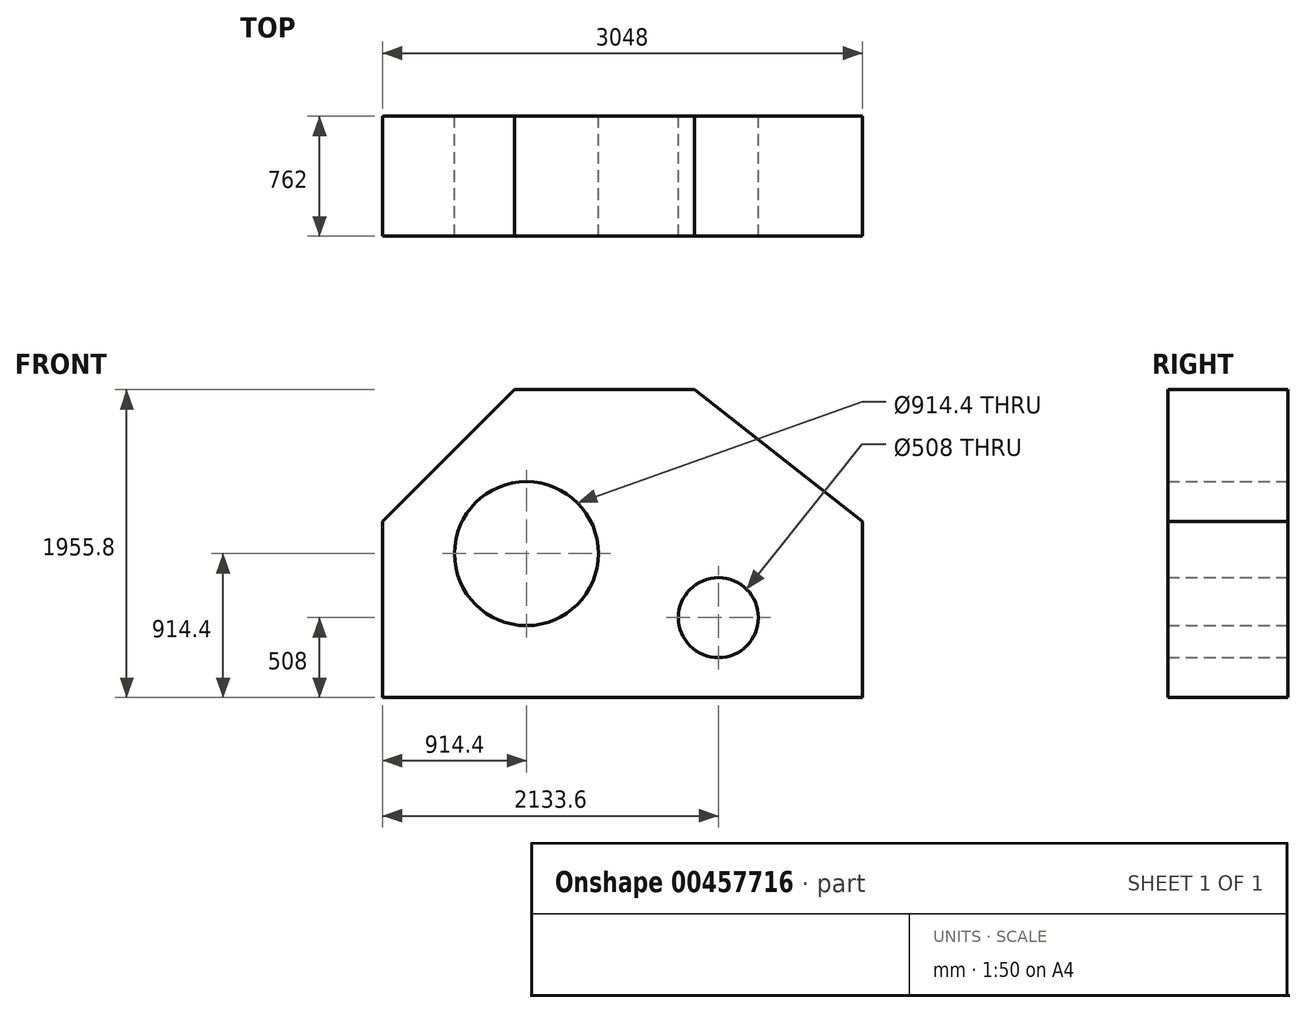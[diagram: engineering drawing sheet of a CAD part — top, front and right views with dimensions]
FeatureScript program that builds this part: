
annotation { "Feature Type Name" : "Feature", "Feature Type Description" : "" }
export const myFeature = defineFeature(function(context is Context, id is Id, definition is map)
    precondition{}
    {
        {
            var Q0;
            Q0=qCreatedBy(makeId("Front.planeOp"),FACE);
            var sketch = newSketch(context, id + "F0", { "sketchPlane" : qUnion([Q0])});
            skLineSegment(sketch, "E0", {"start": v(0, 0) * mm, "end": v(3048, 0) * mm});
            skLineSegment(sketch, "E1", {"start": v(3048, 0) * mm, "end": v(3048, 1117.6) * mm});
            skLineSegment(sketch, "E2", {"start": v(0, 0) * mm, "end": v(0, 1117.6) * mm});
            skLineSegment(sketch, "E3", {"start": v(0, 1117.6) * mm, "end": v(838.2, 1955.8) * mm});
            skLineSegment(sketch, "E4", {"start": v(838.2, 1955.8) * mm, "end": v(1981.2, 1955.8) * mm});
            skLineSegment(sketch, "E5", {"start": v(1981.2, 1955.8) * mm, "end": v(3048, 1117.6) * mm});
            skCircle(sketch, "E6", {"center": v(914.4, 914.4) * mm, "radius": 457.2 * mm});
            skCircle(sketch, "E7", {"center": v(2133.6, 508) * mm, "radius": 254 * mm});
            skSolve(sketch);
        }
        {
            var Q0;
            Q0 = qSketchRegion(id + "F0", true);
            extrude(context, id + "F1", {"entities" : qUnion([Q0]), "depth" : 762 * mm});
        }
    });
